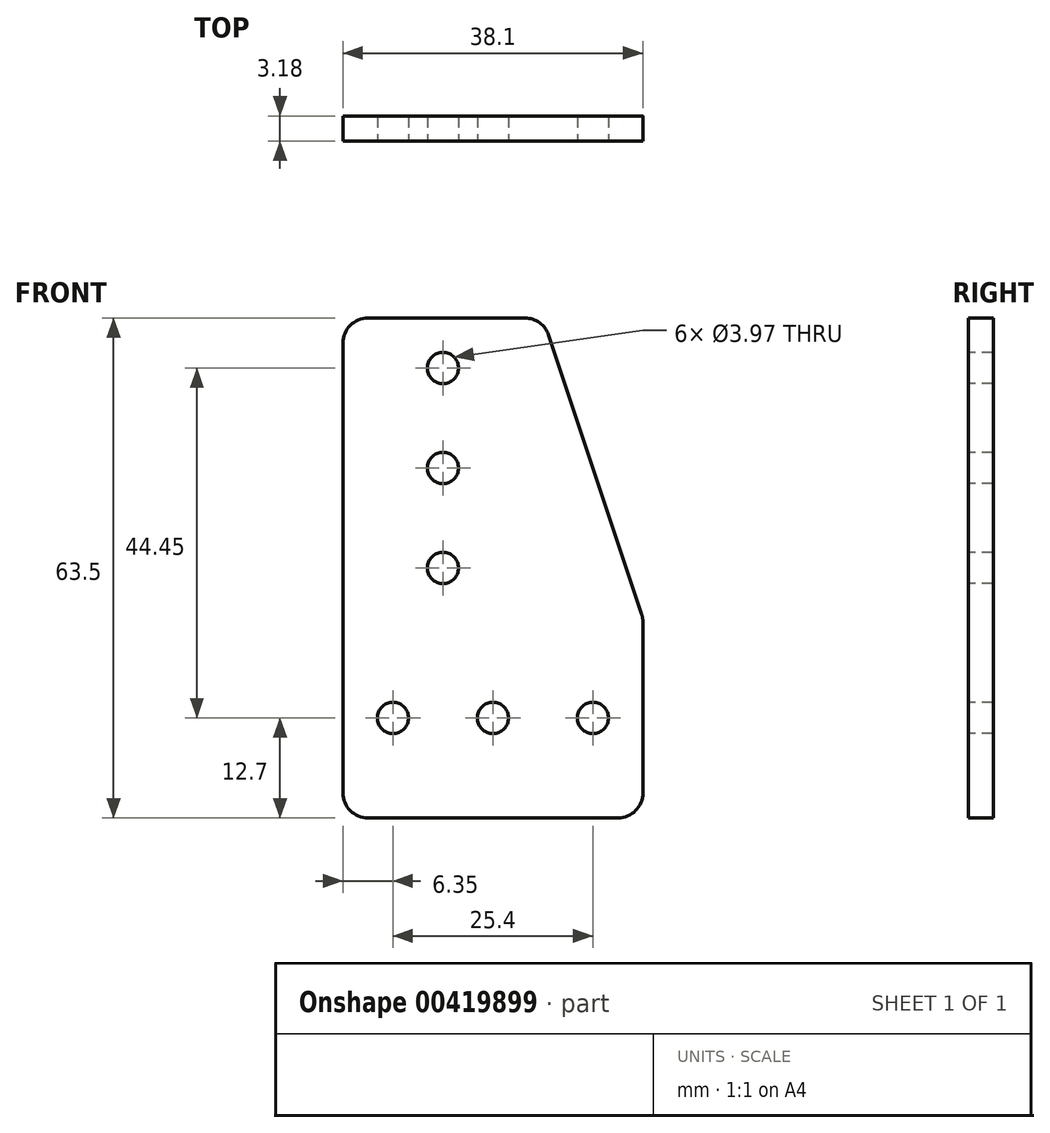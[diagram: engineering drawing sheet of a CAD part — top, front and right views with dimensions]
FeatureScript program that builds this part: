
annotation { "Feature Type Name" : "Feature", "Feature Type Description" : "" }
export const myFeature = defineFeature(function(context is Context, id is Id, definition is map)
    precondition{}
    {
        {
            var Q0;
            Q0=qCreatedBy(makeId("Front.planeOp"),FACE);
            var sketch = newSketch(context, id + "F0", { "sketchPlane" : qUnion([Q0])});
            skLineSegment(sketch, "E0.bottom", {"start": v(4.06, 31.75) * mm, "end": v(-15.88, 31.75) * mm});
            skLineSegment(sketch, "E0.top", {"start": v(15.88, -31.75) * mm, "end": v(-15.87, -31.75) * mm});
            skLineSegment(sketch, "E0.left", {"start": v(19.05, -6.87) * mm, "end": v(19.05, -28.57) * mm});
            skLineSegment(sketch, "E0.right", {"start": v(-19.05, 28.58) * mm, "end": v(-19.05, -28.57) * mm});
            skPoint(sketch, "E0.middle", {"position": v(0, 0) * mm});
            skPoint(sketch, "E1.visualSharp", {"position": v(-19.05, -31.75) * mm});
            skArc(sketch, "E1.filletArc", {"start": v(-19.05, -28.57) * mm, "mid": v(-18.12, -30.82) * mm, "end": v(-15.87, -31.75) * mm});
            skLineSegment(sketch, "E2", {"start": v(7.07, 29.58) * mm, "end": v(18.89, -5.86) * mm});
            skPoint(sketch, "E3.orphan", {"position": v(19.05, 31.75) * mm});
            skPoint(sketch, "E4.visualSharp", {"position": v(-19.05, 31.75) * mm});
            skArc(sketch, "E4.filletArc", {"start": v(-15.88, 31.75) * mm, "mid": v(-18.12, 30.82) * mm, "end": v(-19.05, 28.58) * mm});
            skPoint(sketch, "E5.visualSharp", {"position": v(19.05, -31.75) * mm});
            skArc(sketch, "E5.filletArc", {"start": v(15.88, -31.75) * mm, "mid": v(18.12, -30.82) * mm, "end": v(19.05, -28.57) * mm});
            skPoint(sketch, "E6.visualSharp", {"position": v(6.35, 31.75) * mm});
            skArc(sketch, "E6.filletArc", {"start": v(7.07, 29.58) * mm, "mid": v(5.92, 31.15) * mm, "end": v(4.06, 31.75) * mm});
            skPoint(sketch, "E7.visualSharp", {"position": v(19.05, -6.35) * mm});
            skArc(sketch, "E7.filletArc", {"start": v(19.05, -6.87) * mm, "mid": v(19, -6.36) * mm, "end": v(18.89, -5.86) * mm});
            skSolve(sketch);
        }
        {
            var Q0;
            Q0=makeQuery(id+"F0.imprint","IMPRINT",FACE,{"disambiguationData":[TD([[makeQuery(id+"F0.imprint","IMPRINT",EDGE,{"derivedFrom":sQuery(id+"F0.wireOp",EDGE,"E0.bottom")}),1.0]])]});
            extrude(context, id + "F1", {"entities" : qUnion([Q0]), "depth" : 3.17 * mm});
        }
        {
            var Q0;
            Q0=makeQuery(id+"F1.opExtrude","CAP_FACE",FACE,{"disambiguationData":[OSD([sQuery(id+"F0.wireOp",EDGE,"E0.bottom"),sQuery(id+"F0.wireOp",EDGE,"E0.top"),sQuery(id+"F0.wireOp",EDGE,"E0.left"),sQuery(id+"F0.wireOp",EDGE,"E0.right"),sQuery(id+"F0.wireOp",EDGE,"E1.filletArc"),sQuery(id+"F0.wireOp",EDGE,"E2"),sQuery(id+"F0.wireOp",EDGE,"E4.filletArc"),sQuery(id+"F0.wireOp",EDGE,"E5.filletArc"),sQuery(id+"F0.wireOp",EDGE,"E6.filletArc"),sQuery(id+"F0.wireOp",EDGE,"E7.filletArc")])],"isStart":false});
            var sketch = newSketch(context, id + "F2", { "sketchPlane" : qUnion([Q0])});
            skCircle(sketch, "E8", {"center": v(-6.35, 25.4) * mm, "radius": 1.98 * mm});
            skCircle(sketch, "E9", {"center": v(-6.35, 12.7) * mm, "radius": 1.98 * mm});
            skCircle(sketch, "E10", {"center": v(-12.7, -19.05) * mm, "radius": 1.98 * mm});
            skCircle(sketch, "E11", {"center": v(0, -19.05) * mm, "radius": 1.98 * mm});
            skCircle(sketch, "E12", {"center": v(12.7, -19.05) * mm, "radius": 1.98 * mm});
            skCircle(sketch, "E13", {"center": v(-6.35, 0) * mm, "radius": 1.98 * mm});
            skSolve(sketch);
        }
        {
            var Q0;
            Q0=sQuery(id+"F2.wireOp",VERTEX,"E8.center");
            var Q1;
            Q1=sQuery(id+"F2.wireOp",VERTEX,"E9.center");
            var Q2;
            Q2=sQuery(id+"F2.wireOp",VERTEX,"E13.center");
            var Q3;
            Q3=sQuery(id+"F2.wireOp",VERTEX,"E10.center");
            var Q4;
            Q4=sQuery(id+"F2.wireOp",VERTEX,"E11.center");
            var Q5;
            Q5=sQuery(id+"F2.wireOp",VERTEX,"E12.center");
            var Q6;
            Q6=makeQuery(id+"F1.opExtrude","SWEPT_BODY",BODY,{"disambiguationData":[OSD([sQuery(id+"F0.wireOp",EDGE,"E0.bottom"),sQuery(id+"F0.wireOp",EDGE,"E0.top"),sQuery(id+"F0.wireOp",EDGE,"E0.left"),sQuery(id+"F0.wireOp",EDGE,"E0.right"),sQuery(id+"F0.wireOp",EDGE,"E1.filletArc"),sQuery(id+"F0.wireOp",EDGE,"E2"),sQuery(id+"F0.wireOp",EDGE,"E4.filletArc"),sQuery(id+"F0.wireOp",EDGE,"E5.filletArc"),sQuery(id+"F0.wireOp",EDGE,"E6.filletArc"),sQuery(id+"F0.wireOp",EDGE,"E7.filletArc")])]});
            hole(context, id + "F3", {"style" : HoleStyle.SIMPLE, "endStyle" : HoleEndStyle.THROUGH, "holeDiameter" : 3.97 * mm, "isTappedThrough" : true, "tappedDepth" : 12.7 * mm, "tapClearance" : 3, "locations" : qUnion([Q0, Q1, Q2, Q3, Q4, Q5]), "scope" : qUnion([Q6])});
        }
    });
